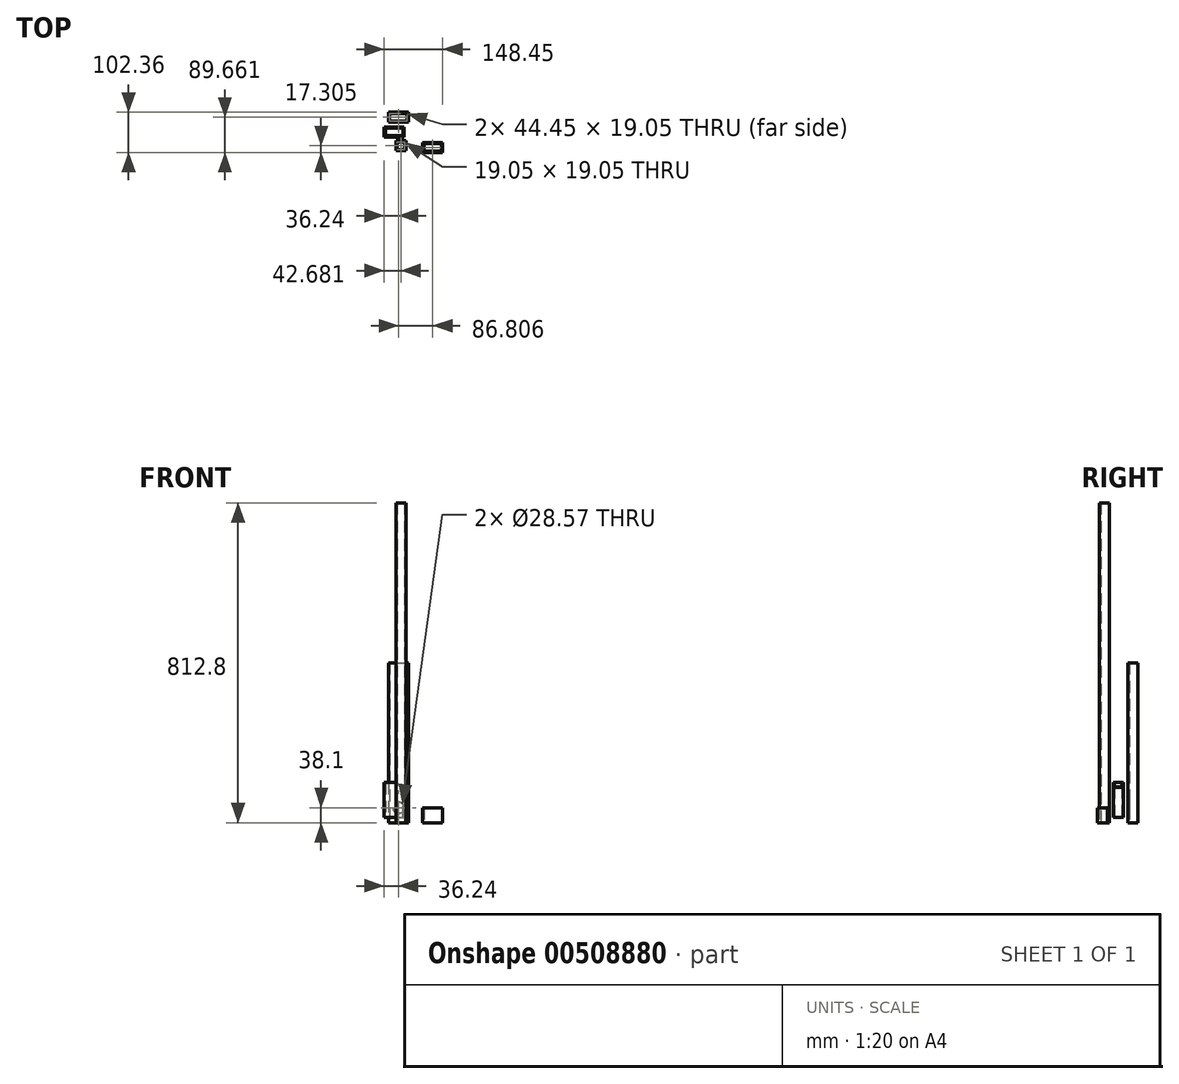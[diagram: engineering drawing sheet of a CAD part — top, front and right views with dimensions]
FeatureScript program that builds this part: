
annotation { "Feature Type Name" : "Feature", "Feature Type Description" : "" }
export const myFeature = defineFeature(function(context is Context, id is Id, definition is map)
    precondition{}
    {
        {
            var Q0;
            Q0=qCreatedBy(makeId("Front.planeOp"),FACE);
            var sketch = newSketch(context, id + "F0", { "sketchPlane" : qUnion([Q0])});
            skLineSegment(sketch, "E0", {"start": v(-82.83, 101.95) * mm, "end": v(-82.83, 13.05) * mm});
            skLineSegment(sketch, "E1", {"start": v(-82.83, 13.05) * mm, "end": v(-32.03, 13.05) * mm});
            skLineSegment(sketch, "E2", {"start": v(-32.03, 13.05) * mm, "end": v(-32.03, 89.25) * mm});
            skLineSegment(sketch, "E3", {"start": v(-32.03, 89.25) * mm, "end": v(-57.43, 101.95) * mm});
            skLineSegment(sketch, "E4", {"start": v(-82.83, 101.95) * mm, "end": v(-57.43, 101.95) * mm});
            skSolve(sketch);
        }
        {
            var Q0;
            Q0=makeQuery(id+"F0.imprint","IMPRINT",FACE,{"disambiguationData":[TD([[makeQuery(id+"F0.imprint","IMPRINT",EDGE,{"derivedFrom":sQuery(id+"F0.wireOp",EDGE,"E0")}),1.0]])]});
            extrude(context, id + "F1", {"entities" : qUnion([Q0]), "depth" : 25.4 * mm});
        }
        {
            var Q0;
            Q0=makeQuery(id+"F1.opExtrude","SWEPT_FACE",FACE,{"disambiguationData":[OSD([sQuery(id+"F0.wireOp",EDGE,"E3")])]});
            var Q1;
            Q1=makeQuery(id+"F1.opExtrude","SWEPT_FACE",FACE,{"disambiguationData":[OSD([sQuery(id+"F0.wireOp",EDGE,"E4")])]});
            var Q2;
            Q2=makeQuery(id+"F1.opExtrude","SWEPT_FACE",FACE,{"disambiguationData":[OSD([sQuery(id+"F0.wireOp",EDGE,"E1")])]});
            shell(context, id + "F2", {"entities" : qUnion([Q0, Q1, Q2]), "thickness" : 3.17 * mm});
        }
        {
            var Q0;
            Q0=qCreatedBy(makeId("Top.planeOp"),FACE);
            var sketch = newSketch(context, id + "F3", { "sketchPlane" : qUnion([Q0])});
            skLineSegment(sketch, "E5.bottom", {"start": v(-52.85, -34.88) * mm, "end": v(-27.45, -34.88) * mm});
            skLineSegment(sketch, "E5.top", {"start": v(-52.85, -60.28) * mm, "end": v(-27.45, -60.28) * mm});
            skLineSegment(sketch, "E5.left", {"start": v(-52.85, -34.88) * mm, "end": v(-52.85, -60.28) * mm});
            skLineSegment(sketch, "E5.right", {"start": v(-27.45, -34.88) * mm, "end": v(-27.45, -60.28) * mm});
            skPoint(sketch, "E5.middle", {"position": v(-40.15, -47.58) * mm});
            skSolve(sketch);
        }
        {
            var Q0;
            Q0=makeQuery(id+"F3.imprint","IMPRINT",FACE,{"disambiguationData":[TD([[makeQuery(id+"F3.imprint","IMPRINT",EDGE,{"derivedFrom":sQuery(id+"F3.wireOp",EDGE,"E5.bottom")}),-1.0]])]});
            extrude(context, id + "F4", {"entities" : qUnion([Q0]), "depth" : 812.8 * mm});
        }
        {
            var Q0;
            Q0=makeQuery(id+"F4.opExtrude","CAP_FACE",FACE,{"disambiguationData":[OSD([sQuery(id+"F3.wireOp",EDGE,"E5.bottom"),sQuery(id+"F3.wireOp",EDGE,"E5.top"),sQuery(id+"F3.wireOp",EDGE,"E5.left"),sQuery(id+"F3.wireOp",EDGE,"E5.right")])],"isStart":false});
            var Q1;
            Q1=makeQuery(id+"F4.opExtrude","CAP_FACE",FACE,{"disambiguationData":[OSD([sQuery(id+"F3.wireOp",EDGE,"E5.bottom"),sQuery(id+"F3.wireOp",EDGE,"E5.top"),sQuery(id+"F3.wireOp",EDGE,"E5.left"),sQuery(id+"F3.wireOp",EDGE,"E5.right")])],"isStart":true});
            shell(context, id + "F5", {"entities" : qUnion([Q0, Q1]), "thickness" : 3.17 * mm});
        }
        {
            var Q0;
            Q0=qCreatedBy(makeId("Top.planeOp"),FACE);
            var sketch = newSketch(context, id + "F6", { "sketchPlane" : qUnion([Q0])});
            skLineSegment(sketch, "E6.bottom", {"start": v(65.62, -64.88) * mm, "end": v(14.82, -64.88) * mm});
            skLineSegment(sketch, "E6.top", {"start": v(65.62, -39.48) * mm, "end": v(14.82, -39.48) * mm});
            skLineSegment(sketch, "E6.left", {"start": v(65.62, -64.88) * mm, "end": v(65.62, -39.48) * mm});
            skLineSegment(sketch, "E6.right", {"start": v(14.82, -64.88) * mm, "end": v(14.82, -39.48) * mm});
            skPoint(sketch, "E6.middle", {"position": v(40.22, -52.18) * mm});
            skSolve(sketch);
        }
        {
            var Q0;
            Q0=makeQuery(id+"F6.imprint","IMPRINT",FACE,{"disambiguationData":[TD([[makeQuery(id+"F6.imprint","IMPRINT",EDGE,{"derivedFrom":sQuery(id+"F6.wireOp",EDGE,"E6.bottom")}),-1.0]])]});
            extrude(context, id + "F7", {"entities" : qUnion([Q0]), "depth" : 38.1 * mm});
        }
        {
            var Q0;
            Q0=makeQuery(id+"F7.opExtrude","CAP_FACE",FACE,{"disambiguationData":[OSD([sQuery(id+"F6.wireOp",EDGE,"E6.bottom"),sQuery(id+"F6.wireOp",EDGE,"E6.top"),sQuery(id+"F6.wireOp",EDGE,"E6.left"),sQuery(id+"F6.wireOp",EDGE,"E6.right")])],"isStart":false});
            var Q1;
            Q1=makeQuery(id+"F7.opExtrude","CAP_FACE",FACE,{"disambiguationData":[OSD([sQuery(id+"F6.wireOp",EDGE,"E6.bottom"),sQuery(id+"F6.wireOp",EDGE,"E6.top"),sQuery(id+"F6.wireOp",EDGE,"E6.left"),sQuery(id+"F6.wireOp",EDGE,"E6.right")])],"isStart":true});
            shell(context, id + "F8", {"entities" : qUnion([Q0, Q1]), "thickness" : 3.17 * mm});
        }
        {
            var Q0;
            Q0=qCreatedBy(makeId("Top.planeOp"),FACE);
            var sketch = newSketch(context, id + "F9", { "sketchPlane" : qUnion([Q0])});
            skLineSegment(sketch, "E7.bottom", {"start": v(-72, 37.48) * mm, "end": v(-21.2, 37.48) * mm});
            skLineSegment(sketch, "E7.top", {"start": v(-72, 12.08) * mm, "end": v(-21.2, 12.08) * mm});
            skLineSegment(sketch, "E7.left", {"start": v(-72, 37.48) * mm, "end": v(-72, 12.08) * mm});
            skLineSegment(sketch, "E7.right", {"start": v(-21.2, 37.48) * mm, "end": v(-21.2, 12.08) * mm});
            skPoint(sketch, "E7.middle", {"position": v(-46.6, 24.78) * mm});
            skSolve(sketch);
        }
        {
            var Q0;
            Q0=makeQuery(id+"F9.imprint","IMPRINT",FACE,{"disambiguationData":[TD([[makeQuery(id+"F9.imprint","IMPRINT",EDGE,{"derivedFrom":sQuery(id+"F9.wireOp",EDGE,"E7.bottom")}),-1.0]])]});
            extrude(context, id + "F10", {"entities" : qUnion([Q0]), "depth" : 406.4 * mm});
        }
        {
            var Q0;
            Q0=makeQuery(id+"F10.opExtrude","CAP_FACE",FACE,{"disambiguationData":[OSD([sQuery(id+"F9.wireOp",EDGE,"E7.bottom"),sQuery(id+"F9.wireOp",EDGE,"E7.top"),sQuery(id+"F9.wireOp",EDGE,"E7.left"),sQuery(id+"F9.wireOp",EDGE,"E7.right")])],"isStart":false});
            var Q1;
            Q1=makeQuery(id+"F10.opExtrude","CAP_FACE",FACE,{"disambiguationData":[OSD([sQuery(id+"F9.wireOp",EDGE,"E7.bottom"),sQuery(id+"F9.wireOp",EDGE,"E7.top"),sQuery(id+"F9.wireOp",EDGE,"E7.left"),sQuery(id+"F9.wireOp",EDGE,"E7.right")])],"isStart":true});
            shell(context, id + "F11", {"entities" : qUnion([Q0, Q1]), "thickness" : 3.17 * mm});
        }
        {
            var Q0;
            Q0=makeQuery(id+"F10.opExtrude","SWEPT_FACE",FACE,{"disambiguationData":[OSD([sQuery(id+"F9.wireOp",EDGE,"E7.bottom")])]});
            var sketch = newSketch(context, id + "F12", { "sketchPlane" : qUnion([Q0])});
            skCircle(sketch, "E8", {"center": v(46.6, 38.1) * mm, "radius": 14.29 * mm});
            skPoint(sketch, "E8.centerSnap0", {"position": v(46.6, 0) * mm});
            skPoint(sketch, "E8.perimeterSnap0", {"position": v(46.6, 0) * mm});
            skSolve(sketch);
        }
        {
            var Q0;
            Q0=makeQuery(id+"F12.imprint","IMPRINT",FACE,{"disambiguationData":[TD([[makeQuery(id+"F12.imprint","IMPRINT",EDGE,{"derivedFrom":sQuery(id+"F12.wireOp",EDGE,"E8")}),1.0]])]});
            var Q1;
            Q1=makeQuery(id+"F10.opExtrude","SWEPT_FACE",FACE,{"disambiguationData":[OSD([sQuery(id+"F9.wireOp",EDGE,"E7.top")])]});
            extrude(context, id + "F13", {"entities" : qUnion([Q0]), "operationType" : NewBodyOperationType.REMOVE, "endBound" : BoundingType.UP_TO_SURFACE, "oppositeDirection" : true, "endBoundEntityFace" : qUnion([Q1]), "depth" : 25.4 * mm});
        }
    });
